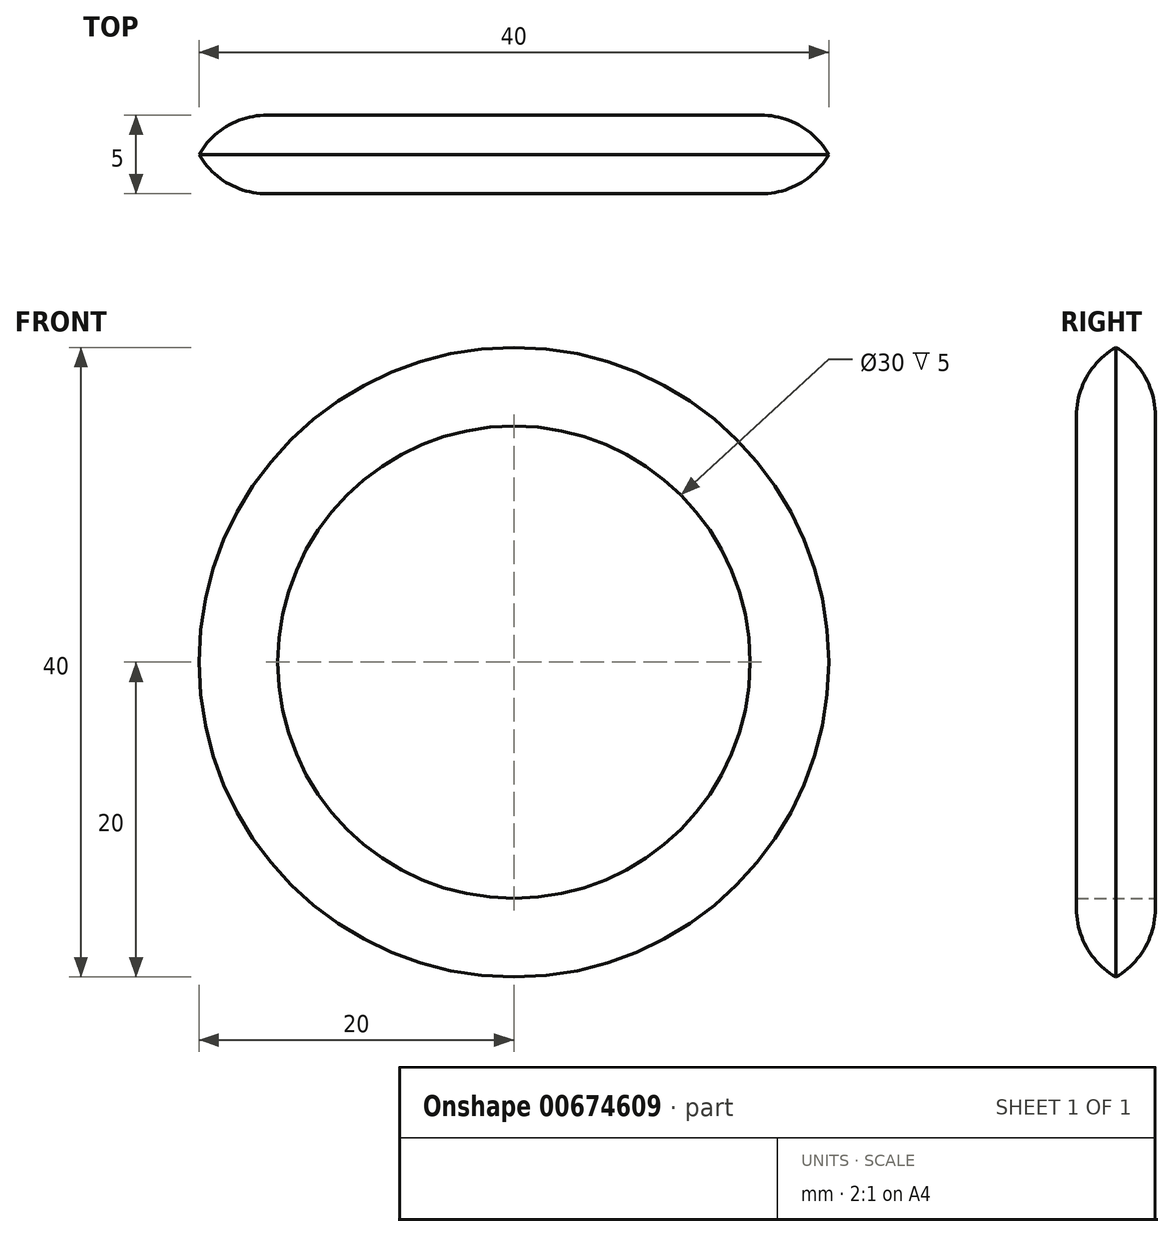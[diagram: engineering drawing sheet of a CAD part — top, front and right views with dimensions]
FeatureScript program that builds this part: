
annotation { "Feature Type Name" : "Feature", "Feature Type Description" : "" }
export const myFeature = defineFeature(function(context is Context, id is Id, definition is map)
    precondition{}
    {
        {
            var Q0;
            Q0=qCreatedBy(makeId("Front.planeOp"),FACE);
            var sketch = newSketch(context, id + "F0", { "sketchPlane" : qUnion([Q0])});
            skCircle(sketch, "E0", {"center": v(0, 0) * mm, "radius": 20 * mm});
            skCircle(sketch, "E1", {"center": v(0, 0) * mm, "radius": 15 * mm});
            skSolve(sketch);
        }
        {
            var Q0;
            Q0 = qSketchRegion(id + "F0", true);
            extrude(context, id + "F1", {"entities" : qUnion([Q0]), "depth" : 2.5 * mm, "offsetDistance" : 25 * mm});
        }
        {
            var Q0;
            Q0=makeQuery(id+"F1.opExtrude","CAP_EDGE",EDGE,{"disambiguationData":[OSD([sQuery(id+"F0.wireOp",EDGE,"E0")])],"isStart":false});
            fillet(context, id + "F2", {"entities" : qUnion([Q0]), "radius" : 5 * mm, "tangentPropagation" : true, "allowEdgeOverflow" : false});
        }
        {
            var Q0;
            Q0=makeQuery(id+"F1.opExtrude","SWEPT_BODY",BODY,{"disambiguationData":[OSD([sQuery(id+"F0.wireOp",EDGE,"E0"),sQuery(id+"F0.wireOp",EDGE,"E1")])]});
            var Q1;
            Q1=qCreatedBy(makeId("Front.planeOp"),FACE);
            mirror(context, id + "F3", {"operationType" : NewBodyOperationType.ADD, "entities" : qUnion([Q0]), "mirrorPlane" : qUnion([Q1])});
        }
    });
